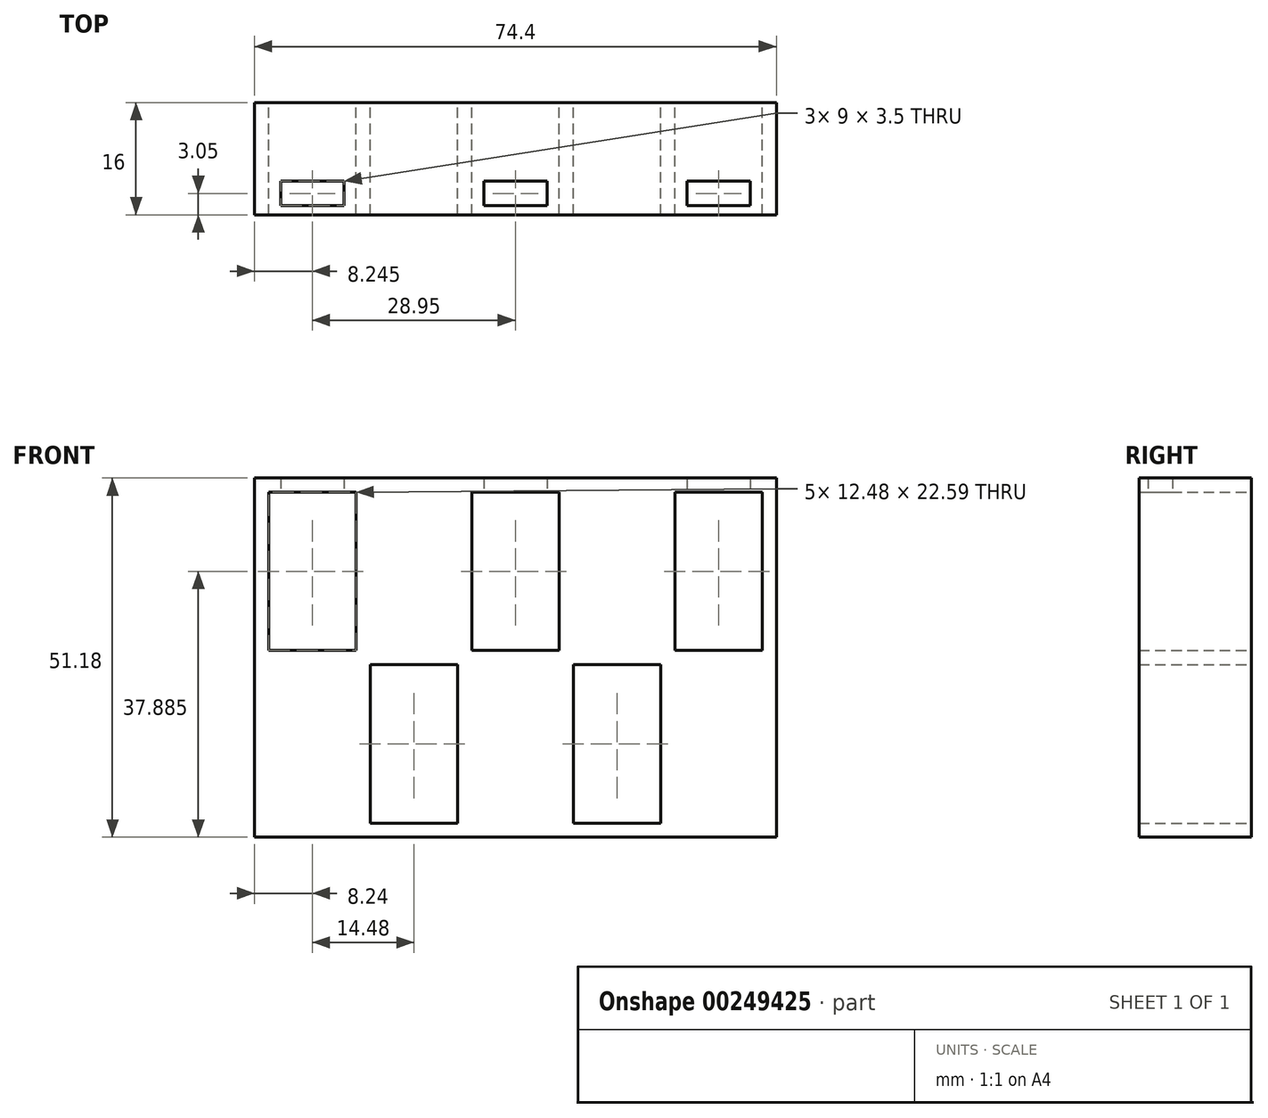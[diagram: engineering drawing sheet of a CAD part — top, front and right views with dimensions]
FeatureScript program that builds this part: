
annotation { "Feature Type Name" : "Feature", "Feature Type Description" : "" }
export const myFeature = defineFeature(function(context is Context, id is Id, definition is map)
    precondition{}
    {
        {
            var Q0;
            Q0=qCreatedBy(makeId("Front.planeOp"),FACE);
            var sketch = newSketch(context, id + "F0", { "sketchPlane" : qUnion([Q0])});
            skLineSegment(sketch, "E0.bottom", {"start": v(-8.24, -23.59) * mm, "end": v(-20.72, -23.59) * mm});
            skLineSegment(sketch, "E0.top", {"start": v(-8.24, -1) * mm, "end": v(-20.72, -1) * mm});
            skLineSegment(sketch, "E0.left", {"start": v(-8.24, -23.59) * mm, "end": v(-8.24, -1) * mm});
            skLineSegment(sketch, "E0.right", {"start": v(-20.72, -23.59) * mm, "end": v(-20.72, -1) * mm});
            skPoint(sketch, "E0.middle", {"position": v(-14.48, -12.3) * mm});
            skLineSegment(sketch, "E1.bottom", {"start": v(6.24, 1) * mm, "end": v(-6.24, 1) * mm});
            skLineSegment(sketch, "E1.top", {"start": v(6.24, 23.59) * mm, "end": v(-6.24, 23.59) * mm});
            skLineSegment(sketch, "E1.left", {"start": v(6.24, 1) * mm, "end": v(6.24, 23.59) * mm});
            skLineSegment(sketch, "E1.right", {"start": v(-6.24, 1) * mm, "end": v(-6.24, 23.59) * mm});
            skPoint(sketch, "E1.middle", {"position": v(0, 12.3) * mm});
            skLineSegment(sketch, "E2.bottom", {"start": v(20.72, -23.6) * mm, "end": v(8.24, -23.6) * mm});
            skLineSegment(sketch, "E2.top", {"start": v(20.72, -1) * mm, "end": v(8.24, -1) * mm});
            skLineSegment(sketch, "E2.left", {"start": v(20.72, -23.59) * mm, "end": v(20.72, -1) * mm});
            skLineSegment(sketch, "E2.right", {"start": v(8.24, -23.6) * mm, "end": v(8.24, -1) * mm});
            skPoint(sketch, "E2.middle", {"position": v(14.48, -12.3) * mm});
            skLineSegment(sketch, "E3.bottom", {"start": v(35.2, 1) * mm, "end": v(22.72, 1) * mm});
            skLineSegment(sketch, "E3.top", {"start": v(35.2, 23.59) * mm, "end": v(22.72, 23.59) * mm});
            skLineSegment(sketch, "E3.left", {"start": v(35.2, 1) * mm, "end": v(35.2, 23.59) * mm});
            skLineSegment(sketch, "E3.right", {"start": v(22.72, 1) * mm, "end": v(22.72, 23.59) * mm});
            skPoint(sketch, "E3.middle", {"position": v(28.96, 12.3) * mm});
            skLineSegment(sketch, "E4.bottom", {"start": v(-22.72, 1) * mm, "end": v(-35.2, 1) * mm});
            skLineSegment(sketch, "E4.top", {"start": v(-22.72, 23.59) * mm, "end": v(-35.2, 23.59) * mm});
            skLineSegment(sketch, "E4.left", {"start": v(-22.72, 1) * mm, "end": v(-22.72, 23.59) * mm});
            skLineSegment(sketch, "E4.right", {"start": v(-35.2, 1) * mm, "end": v(-35.2, 23.59) * mm});
            skPoint(sketch, "E4.middle", {"position": v(-28.96, 12.3) * mm});
            skLineSegment(sketch, "E5.bottom", {"start": v(-152.4, 139.3) * mm, "end": v(152.4, 139.3) * mm, "construction": true});
            skLineSegment(sketch, "E5.top", {"start": v(-152.4, -114.7) * mm, "end": v(152.4, -114.7) * mm, "construction": true});
            skLineSegment(sketch, "E5.left", {"start": v(-152.4, 139.3) * mm, "end": v(-152.4, -114.7) * mm, "construction": true});
            skLineSegment(sketch, "E5.right", {"start": v(152.4, 139.3) * mm, "end": v(152.4, -114.7) * mm, "construction": true});
            skLineSegment(sketch, "E6.bottom", {"start": v(35.2, -23.6) * mm, "end": v(-35.2, -23.6) * mm, "construction": true});
            skLineSegment(sketch, "E6.top", {"start": v(35.2, 23.59) * mm, "end": v(-35.2, 23.59) * mm, "construction": true});
            skLineSegment(sketch, "E6.left", {"start": v(35.2, -23.59) * mm, "end": v(35.2, 23.59) * mm, "construction": true});
            skLineSegment(sketch, "E6.right", {"start": v(-35.2, -23.6) * mm, "end": v(-35.2, 23.59) * mm, "construction": true});
            skPoint(sketch, "E7", {"position": v(0, 0) * mm});
            skLineSegment(sketch, "E8.bottom", {"start": v(-37.2, 25.6) * mm, "end": v(37.2, 25.6) * mm});
            skLineSegment(sketch, "E8.top", {"start": v(-37.2, -25.6) * mm, "end": v(37.2, -25.6) * mm});
            skLineSegment(sketch, "E8.left", {"start": v(-37.2, 25.6) * mm, "end": v(-37.2, -25.6) * mm});
            skLineSegment(sketch, "E8.right", {"start": v(37.2, 25.6) * mm, "end": v(37.2, -25.6) * mm});
            skSolve(sketch);
        }
        {
            var Q0;
            Q0=makeQuery(id+"F0.imprint","IMPRINT",FACE,{"disambiguationData":[TD([[makeQuery(id+"F0.imprint","IMPRINT",EDGE,{"derivedFrom":sQuery(id+"F0.wireOp",EDGE,"E0.bottom")}),1.0]])]});
            extrude(context, id + "F1", {"entities" : qUnion([Q0]), "depth" : 16 * mm});
        }
        {
            var Q0;
            Q0=makeQuery(id+"F1.opExtrude","SWEPT_FACE",FACE,{"disambiguationData":[OSD([sQuery(id+"F0.wireOp",EDGE,"E4.top")])]});
            var sketch = newSketch(context, id + "F2", { "sketchPlane" : qUnion([Q0])});
            skLineSegment(sketch, "E9.0.1", {"start": v(-35.2, 0) * mm, "end": v(-35.2, 16) * mm});
            skLineSegment(sketch, "E9.0.3", {"start": v(-35.2, 16) * mm, "end": v(-35.2, 0) * mm});
            skLineSegment(sketch, "E10.0", {"start": v(-22.72, 16) * mm, "end": v(-22.72, 0) * mm});
            skLineSegment(sketch, "E11.0.1", {"start": v(-22.72, 0) * mm, "end": v(-22.72, 16) * mm});
            skLineSegment(sketch, "E12.0.1", {"start": v(-6.24, 0) * mm, "end": v(-6.24, 16) * mm});
            skLineSegment(sketch, "E12.0.3", {"start": v(-6.24, 16) * mm, "end": v(-6.24, 0) * mm});
            skLineSegment(sketch, "E13.0.1", {"start": v(6.24, 0) * mm, "end": v(6.24, 16) * mm});
            skLineSegment(sketch, "E13.0.3", {"start": v(6.24, 16) * mm, "end": v(6.24, 0) * mm});
            skLineSegment(sketch, "E14.0.1", {"start": v(22.72, 0) * mm, "end": v(22.72, 16) * mm});
            skLineSegment(sketch, "E14.0.3", {"start": v(22.72, 16) * mm, "end": v(22.72, 0) * mm});
            skLineSegment(sketch, "E15.0.1", {"start": v(35.2, 0) * mm, "end": v(35.2, 16) * mm});
            skLineSegment(sketch, "E15.0.3", {"start": v(35.2, 16) * mm, "end": v(35.2, 0) * mm});
            skLineSegment(sketch, "E16.bottom", {"start": v(-33.46, 14.7) * mm, "end": v(-24.46, 14.7) * mm});
            skLineSegment(sketch, "E16.top", {"start": v(-33.46, 11.2) * mm, "end": v(-24.46, 11.2) * mm});
            skLineSegment(sketch, "E16.left", {"start": v(-33.46, 14.7) * mm, "end": v(-33.46, 11.2) * mm});
            skLineSegment(sketch, "E16.right", {"start": v(-24.46, 14.7) * mm, "end": v(-24.46, 11.2) * mm});
            skLineSegment(sketch, "E17", {"start": v(-14.48, -8.46) * mm, "end": v(-14.48, 21.61) * mm});
            skLineSegment(sketch, "E18.MirrorCS", {"start": v(4.5, 11.2) * mm, "end": v(-4.5, 11.2) * mm});
            skLineSegment(sketch, "E19.MirrorCS", {"start": v(-4.5, 14.7) * mm, "end": v(-4.5, 11.2) * mm});
            skLineSegment(sketch, "E20.MirrorCS", {"start": v(4.5, 14.7) * mm, "end": v(-4.5, 14.7) * mm});
            skLineSegment(sketch, "E21.MirrorCS", {"start": v(4.5, 14.7) * mm, "end": v(4.5, 11.2) * mm});
            skLineSegment(sketch, "E22.MirrorCS", {"start": v(33.46, 14.7) * mm, "end": v(24.46, 14.7) * mm});
            skLineSegment(sketch, "E23.MirrorCS", {"start": v(33.46, 14.7) * mm, "end": v(33.46, 11.2) * mm});
            skLineSegment(sketch, "E24.MirrorCS", {"start": v(33.46, 11.2) * mm, "end": v(24.46, 11.2) * mm});
            skLineSegment(sketch, "E25.MirrorCS", {"start": v(24.46, 14.7) * mm, "end": v(24.46, 11.2) * mm});
            skSolve(sketch);
        }
        {
            var Q0;
            Q0=makeQuery(id+"F2.imprint","IMPRINT",FACE,{"disambiguationData":[TD([[makeQuery(id+"F2.imprint","IMPRINT",EDGE,{"derivedFrom":sQuery(id+"F2.wireOp",EDGE,"E18.MirrorCS")}),-1.0]])]});
            var Q1;
            Q1=makeQuery(id+"F2.imprint","IMPRINT",FACE,{"disambiguationData":[TD([[makeQuery(id+"F2.imprint","IMPRINT",EDGE,{"derivedFrom":sQuery(id+"F2.wireOp",EDGE,"E16.bottom")}),-1.0]])]});
            var Q2;
            Q2=makeQuery(id+"F2.imprint","IMPRINT",FACE,{"disambiguationData":[TD([[makeQuery(id+"F2.imprint","IMPRINT",EDGE,{"derivedFrom":sQuery(id+"F2.wireOp",EDGE,"E22.MirrorCS")}),1.0]])]});
            extrude(context, id + "F3", {"entities" : qUnion([Q0, Q1, Q2]), "operationType" : NewBodyOperationType.REMOVE, "oppositeDirection" : true, "depth" : 25 * mm});
        }
    });
